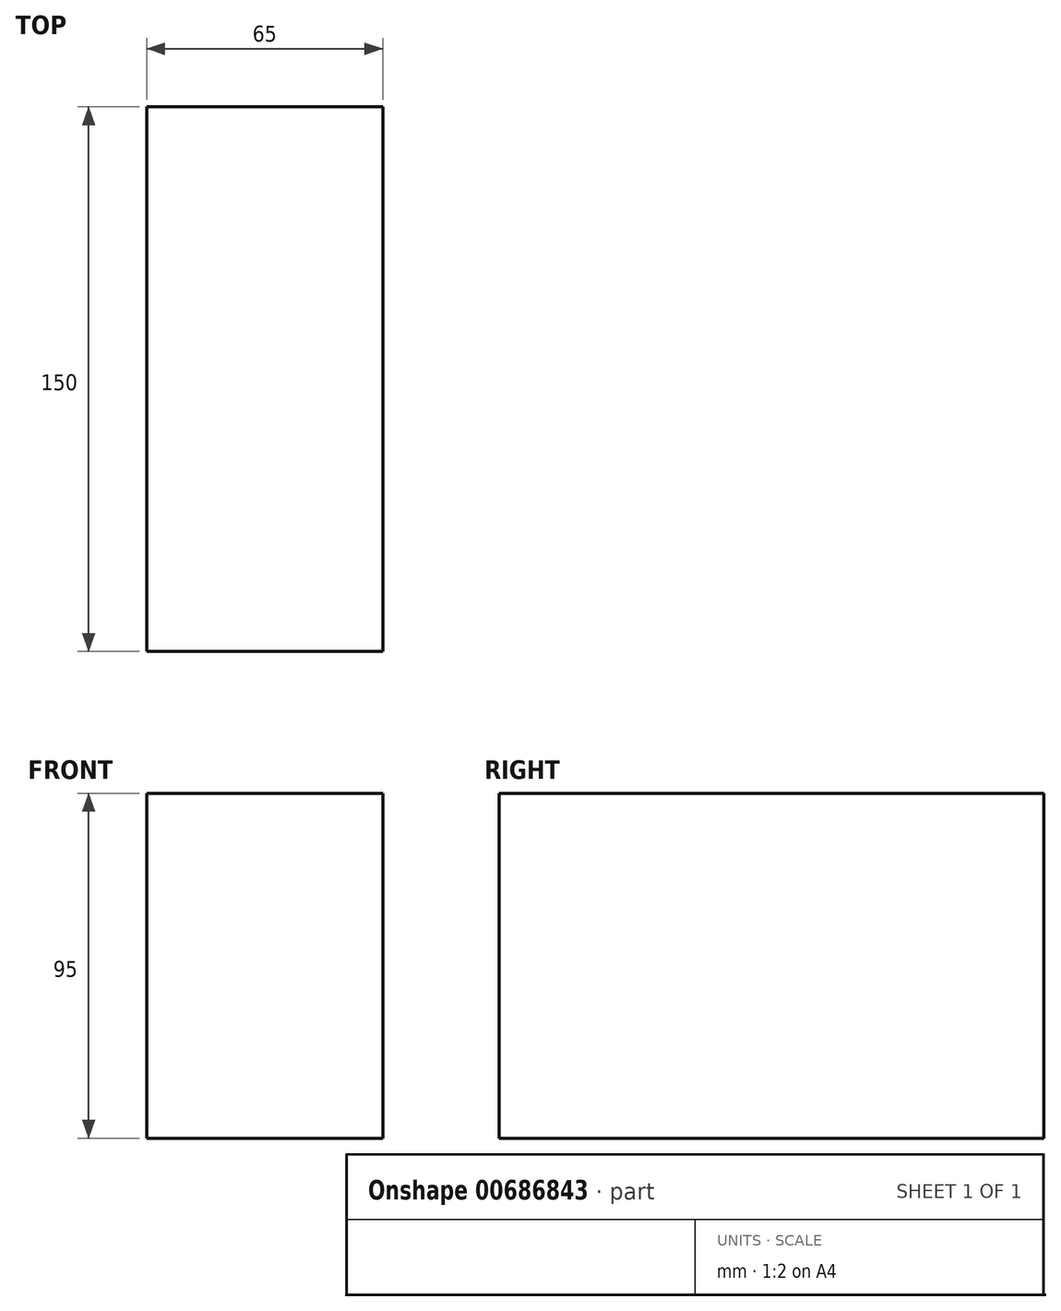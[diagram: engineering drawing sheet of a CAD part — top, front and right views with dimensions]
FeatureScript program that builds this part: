
annotation { "Feature Type Name" : "Feature", "Feature Type Description" : "" }
export const myFeature = defineFeature(function(context is Context, id is Id, definition is map)
    precondition{}
    {
        {
            var Q0;
            Q0=qCreatedBy(makeId("Top.planeOp"),FACE);
            var sketch = newSketch(context, id + "F0", { "sketchPlane" : qUnion([Q0])});
            skLineSegment(sketch, "E0.bottom", {"start": v(-32.5, 75) * mm, "end": v(32.5, 75) * mm});
            skLineSegment(sketch, "E0.top", {"start": v(-32.5, -75) * mm, "end": v(32.5, -75) * mm});
            skLineSegment(sketch, "E0.left", {"start": v(-32.5, 75) * mm, "end": v(-32.5, -75) * mm});
            skLineSegment(sketch, "E0.right", {"start": v(32.5, 75) * mm, "end": v(32.5, -75) * mm});
            skPoint(sketch, "E0.middle", {"position": v(0, 0) * mm});
            skSolve(sketch);
        }
        {
            var Q0;
            Q0=makeQuery(id+"F0.imprint","IMPRINT",FACE,{"disambiguationData":[TD([[makeQuery(id+"F0.imprint","IMPRINT",EDGE,{"derivedFrom":sQuery(id+"F0.wireOp",EDGE,"E0.bottom")}),-1.0]])]});
            extrude(context, id + "F1", {"entities" : qUnion([Q0]), "depth" : 95 * mm, "offsetDistance" : 25 * mm});
        }
    });
